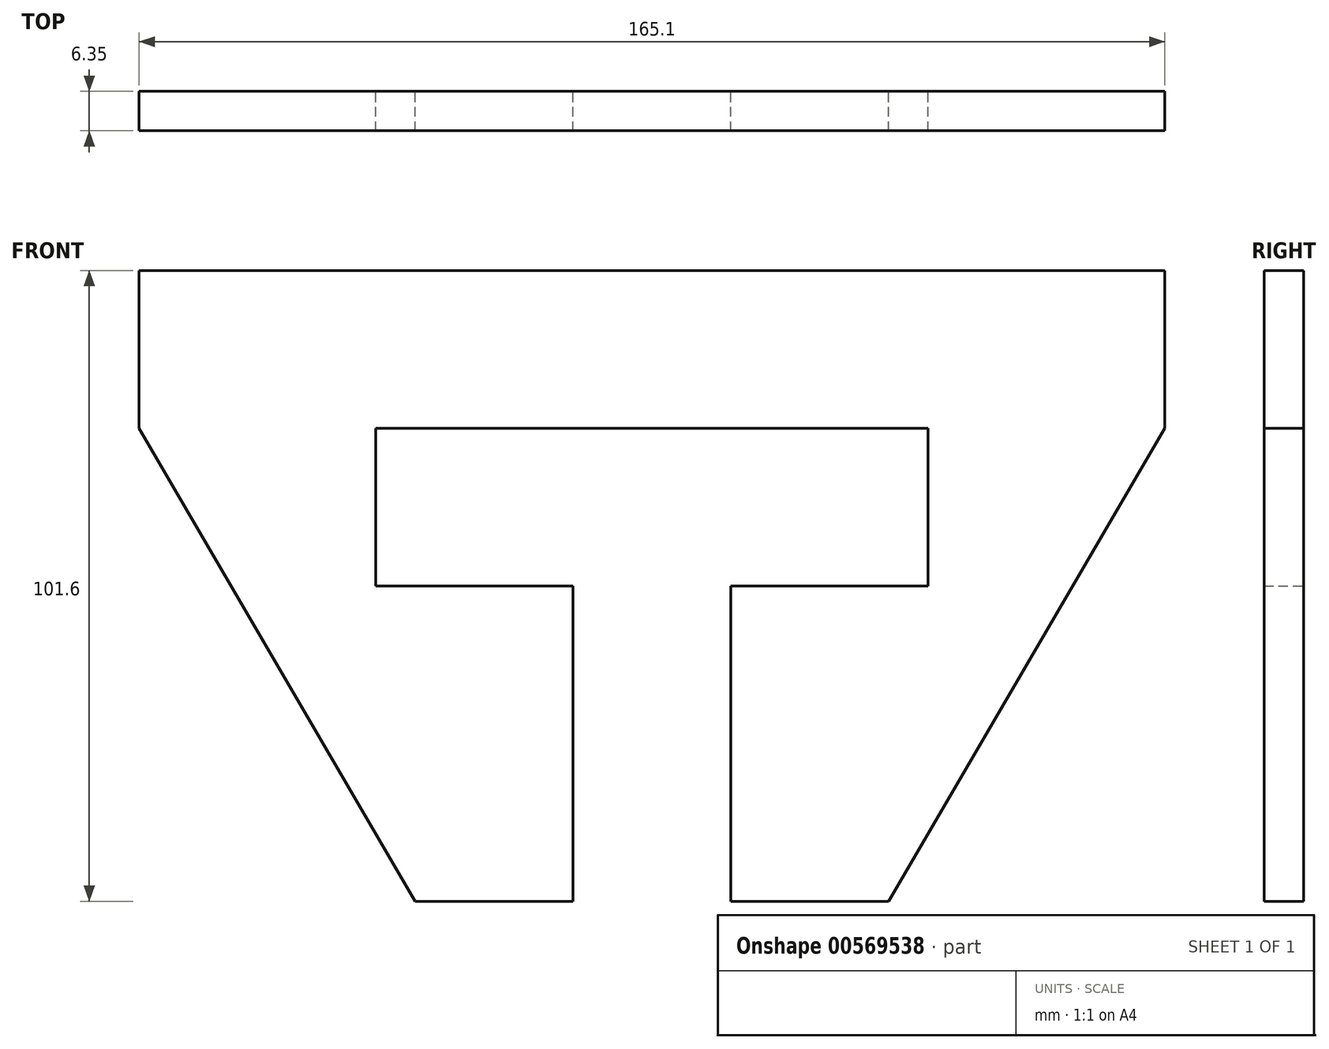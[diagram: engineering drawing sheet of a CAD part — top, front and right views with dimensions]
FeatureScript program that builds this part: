
annotation { "Feature Type Name" : "Feature", "Feature Type Description" : "" }
export const myFeature = defineFeature(function(context is Context, id is Id, definition is map)
    precondition{}
    {
        {
            var Q0;
            Q0=qCreatedBy(makeId("Front.planeOp"),FACE);
            var sketch = newSketch(context, id + "F0", { "sketchPlane" : qUnion([Q0])});
            skLineSegment(sketch, "E0.bottom", {"start": v(44.45, 0) * mm, "end": v(120.65, 0) * mm});
            skLineSegment(sketch, "E0.top", {"start": v(0, 101.6) * mm, "end": v(165.1, 101.6) * mm});
            skLineSegment(sketch, "E0.left", {"start": v(0, 76.2) * mm, "end": v(0, 101.6) * mm});
            skLineSegment(sketch, "E0.right", {"start": v(165.1, 76.2) * mm, "end": v(165.1, 101.6) * mm});
            skLineSegment(sketch, "E1.bottom", {"start": v(0, 101.6) * mm, "end": v(38.1, 101.6) * mm});
            skLineSegment(sketch, "E1.left", {"start": v(0, 101.6) * mm, "end": v(0, 76.2) * mm});
            skLineSegment(sketch, "E2.bottom", {"start": v(38.1, 76.2) * mm, "end": v(127, 76.2) * mm});
            skLineSegment(sketch, "E2.top", {"start": v(38.1, 50.8) * mm, "end": v(127, 50.8) * mm});
            skLineSegment(sketch, "E2.left", {"start": v(38.1, 76.2) * mm, "end": v(38.1, 50.8) * mm});
            skLineSegment(sketch, "E2.right", {"start": v(127, 76.2) * mm, "end": v(127, 50.8) * mm});
            skLineSegment(sketch, "E3", {"start": v(0, 76.2) * mm, "end": v(44.45, 0) * mm});
            skLineSegment(sketch, "E4.bottom", {"start": v(82.55, 50.8) * mm, "end": v(69.85, 50.8) * mm});
            skLineSegment(sketch, "E4.top", {"start": v(82.55, 0) * mm, "end": v(69.85, 0) * mm});
            skLineSegment(sketch, "E4.left", {"start": v(82.55, 50.8) * mm, "end": v(82.55, 0) * mm});
            skLineSegment(sketch, "E4.right", {"start": v(69.85, 50.8) * mm, "end": v(69.85, 0) * mm});
            skLineSegment(sketch, "E5.MirrorCS", {"start": v(95.25, 50.8) * mm, "end": v(95.25, 0) * mm});
            skLineSegment(sketch, "E6.MirrorCS", {"start": v(165.1, 76.2) * mm, "end": v(120.65, 0) * mm});
            skSolve(sketch);
        }
        {
            var Q0;
            Q0=makeQuery(id+"F0.imprint","IMPRINT",FACE,{"disambiguationData":[TD([[makeQuery(id+"F0.imprint","IMPRINT",EDGE,{"derivedFrom":sQuery(id+"F0.wireOp",EDGE,"E0.top")}),-1.0]])]});
            extrude(context, id + "F1", {"entities" : qUnion([Q0]), "depth" : 6.35 * mm, "offsetDistance" : 25.4 * mm});
        }
    });
